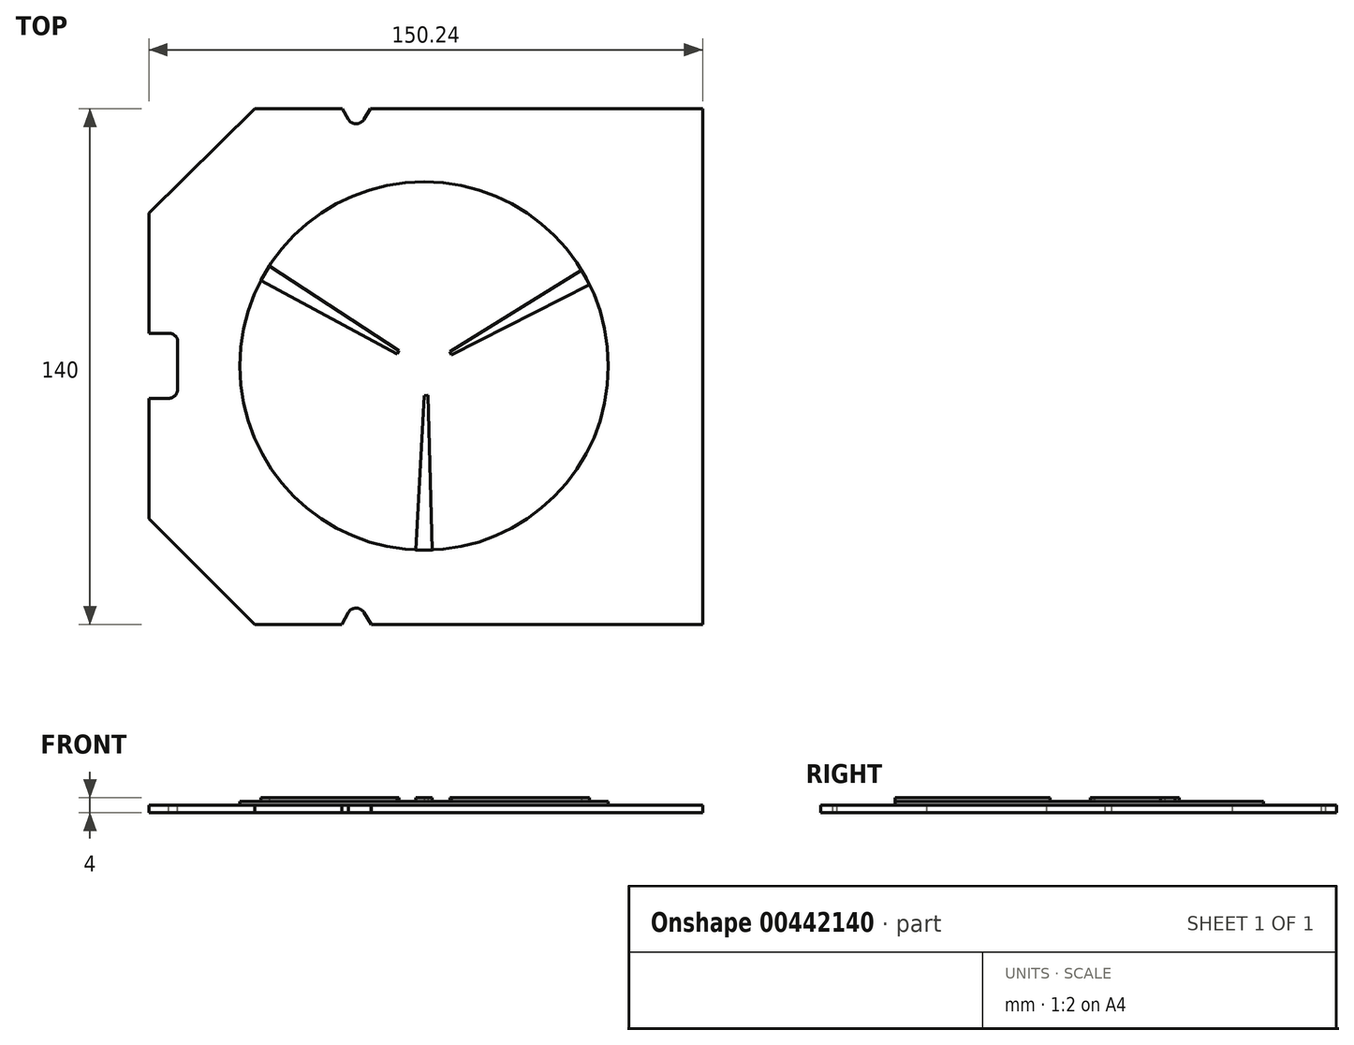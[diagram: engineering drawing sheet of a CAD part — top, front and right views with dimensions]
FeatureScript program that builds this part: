
annotation { "Feature Type Name" : "Feature", "Feature Type Description" : "" }
export const myFeature = defineFeature(function(context is Context, id is Id, definition is map)
    precondition{}
    {
        {
            var Q0;
            Q0=qCreatedBy(makeId("Top.planeOp"),FACE);
            var sketch = newSketch(context, id + "F0", { "sketchPlane" : qUnion([Q0])});
            skLineSegment(sketch, "E0", {"start": v(75.56, 69.8) * mm, "end": v(75.56, -70.2) * mm});
            skLineSegment(sketch, "E1", {"start": v(75.56, -70.2) * mm, "end": v(-45.94, -70.2) * mm});
            skLineSegment(sketch, "E2", {"start": v(-45.94, -70.2) * mm, "end": v(-74.68, -41.47) * mm});
            skLineSegment(sketch, "E3", {"start": v(-74.68, -41.47) * mm, "end": v(-74.68, 41.53) * mm});
            skLineSegment(sketch, "E4", {"start": v(-74.68, 41.53) * mm, "end": v(-45.94, 69.8) * mm});
            skLineSegment(sketch, "E5", {"start": v(-45.94, 69.8) * mm, "end": v(75.56, 69.8) * mm});
            skSolve(sketch);
        }
        {
            var Q0;
            Q0=makeQuery(id+"F0.imprint","IMPRINT",FACE,{"disambiguationData":[TD([[makeQuery(id+"F0.imprint","IMPRINT",EDGE,{"derivedFrom":sQuery(id+"F0.wireOp",EDGE,"E0")}),-1.0]])]});
            extrude(context, id + "F1", {"entities" : qUnion([Q0]), "depth" : 2 * mm});
        }
        {
            var Q0;
            Q0=makeQuery(id+"F1.opExtrude","CAP_FACE",FACE,{"disambiguationData":[OSD([sQuery(id+"F0.wireOp",EDGE,"E0"),sQuery(id+"F0.wireOp",EDGE,"E1"),sQuery(id+"F0.wireOp",EDGE,"E2"),sQuery(id+"F0.wireOp",EDGE,"E3"),sQuery(id+"F0.wireOp",EDGE,"E4"),sQuery(id+"F0.wireOp",EDGE,"E5")])],"isStart":false});
            var sketch = newSketch(context, id + "F2", { "sketchPlane" : qUnion([Q0])});
            skLineSegment(sketch, "E6", {"start": v(-74.68, 8.88) * mm, "end": v(-69.28, 8.88) * mm});
            skLineSegment(sketch, "E7", {"start": v(-74.68, -8.82) * mm, "end": v(-69.28, -8.82) * mm});
            skLineSegment(sketch, "E8", {"start": v(-66.86, 7.04) * mm, "end": v(-66.86, -6.32) * mm});
            skArc(sketch, "E9", {"start": v(-66.86, 7.04) * mm, "mid": v(-67.76, 8.37) * mm, "end": v(-69.28, 8.88) * mm});
            skArc(sketch, "E10", {"start": v(-69.28, -8.82) * mm, "mid": v(-67.56, -8.05) * mm, "end": v(-66.86, -6.32) * mm});
            skLineSegment(sketch, "E11", {"start": v(-74.68, 8.88) * mm, "end": v(-74.68, -8.82) * mm});
            skLineSegment(sketch, "E12", {"start": v(-22.38, -70.2) * mm, "end": v(-20.53, -66.84) * mm});
            skLineSegment(sketch, "E13", {"start": v(-14.31, -70.2) * mm, "end": v(-16.3, -66.92) * mm});
            skArc(sketch, "E14", {"start": v(-16.3, -66.92) * mm, "mid": v(-18.4, -65.72) * mm, "end": v(-20.53, -66.84) * mm});
            skLineSegment(sketch, "E15.MirrorCS", {"start": v(-14.31, 70.2) * mm, "end": v(-16.3, 66.92) * mm});
            skArc(sketch, "E16.MirrorCS", {"start": v(-16.3, 66.92) * mm, "mid": v(-18.4, 65.72) * mm, "end": v(-20.53, 66.84) * mm});
            skLineSegment(sketch, "E17.MirrorCS", {"start": v(-22.38, 70.2) * mm, "end": v(-20.53, 66.84) * mm});
            skLineSegment(sketch, "E18", {"start": v(-22.38, -70.2) * mm, "end": v(-14.31, -70.2) * mm});
            skLineSegment(sketch, "E19", {"start": v(-22.38, 70.2) * mm, "end": v(-14.31, 70.2) * mm});
            skSolve(sketch);
        }
        {
            var Q0;
            Q0=makeQuery(id+"F2.imprint","IMPRINT",FACE,{"disambiguationData":[TD([[makeQuery(id+"F2.imprint","IMPRINT",EDGE,{"derivedFrom":sQuery(id+"F2.wireOp",EDGE,"E6")}),-1.0]])]});
            var Q1;
            Q1=makeQuery(id+"F2.imprint","IMPRINT",FACE,{"disambiguationData":[TD([[makeQuery(id+"F2.imprint","IMPRINT",EDGE,{"derivedFrom":sQuery(id+"F2.wireOp",EDGE,"E15.MirrorCS")}),-1.0]])]});
            var Q2;
            Q2=makeQuery(id+"F2.imprint","IMPRINT",FACE,{"disambiguationData":[TD([[makeQuery(id+"F2.imprint","IMPRINT",EDGE,{"derivedFrom":sQuery(id+"F2.wireOp",EDGE,"E12")}),-1.0]])]});
            extrude(context, id + "F3", {"entities" : qUnion([Q0, Q1, Q2]), "operationType" : NewBodyOperationType.REMOVE, "endBound" : BoundingType.THROUGH_ALL, "oppositeDirection" : true, "depth" : 25 * mm});
        }
        {
            var Q0;
            Q0=makeQuery(id+"F1.opExtrude","CAP_FACE",FACE,{"disambiguationData":[OSD([sQuery(id+"F0.wireOp",EDGE,"E0"),sQuery(id+"F0.wireOp",EDGE,"E1"),sQuery(id+"F0.wireOp",EDGE,"E2"),sQuery(id+"F0.wireOp",EDGE,"E3"),sQuery(id+"F0.wireOp",EDGE,"E4"),sQuery(id+"F0.wireOp",EDGE,"E5")])],"isStart":false});
            var sketch = newSketch(context, id + "F4", { "sketchPlane" : qUnion([Q0])});
            skCircle(sketch, "E20", {"center": v(0, 0) * mm, "radius": 50 * mm});
            skSolve(sketch);
        }
        {
            var Q0;
            Q0 = qSketchRegion(id + "F4", true);
            extrude(context, id + "F5", {"entities" : qUnion([Q0]), "depth" : 1 * mm});
        }
        {
            var Q0;
            Q0=makeQuery(id+"F5.opExtrude","CAP_FACE",FACE,{"disambiguationData":[OSD([sQuery(id+"F4.wireOp",EDGE,"E20")])],"isStart":false});
            var sketch = newSketch(context, id + "F6", { "sketchPlane" : qUnion([Q0])});
            skLineSegment(sketch, "E21", {"start": v(-44.27, 23.24) * mm, "end": v(-7.33, 3.25) * mm});
            skLineSegment(sketch, "E22", {"start": v(-7.33, 3.25) * mm, "end": v(-6.86, 4.13) * mm});
            skLineSegment(sketch, "E23", {"start": v(-6.86, 4.13) * mm, "end": v(-42.02, 27.1) * mm});
            skLineSegment(sketch, "E24", {"start": v(-42.02, 27.1) * mm, "end": v(-44.27, 23.24) * mm});
            skLineSegment(sketch, "E25", {"start": v(-2.24, -49.95) * mm, "end": v(2.24, -49.95) * mm});
            skLineSegment(sketch, "E26", {"start": v(2.24, -49.95) * mm, "end": v(1.07, -7.97) * mm});
            skLineSegment(sketch, "E27", {"start": v(0.08, -8.01) * mm, "end": v(-2.24, -49.95) * mm});
            skLineSegment(sketch, "E28", {"start": v(0.08, -8.01) * mm, "end": v(1.07, -7.97) * mm});
            skLineSegment(sketch, "E29", {"start": v(42.75, 25.94) * mm, "end": v(44.9, 22.01) * mm});
            skLineSegment(sketch, "E30", {"start": v(44.9, 22.01) * mm, "end": v(7.42, 3.05) * mm});
            skLineSegment(sketch, "E31", {"start": v(7.42, 3.05) * mm, "end": v(6.97, 3.94) * mm});
            skLineSegment(sketch, "E32", {"start": v(6.97, 3.94) * mm, "end": v(42.75, 25.94) * mm});
            skSolve(sketch);
        }
        {
            var Q0;
            Q0 = qSketchRegion(id + "F6", true);
            extrude(context, id + "F7", {"entities" : qUnion([Q0]), "depth" : 1 * mm});
        }
    });
